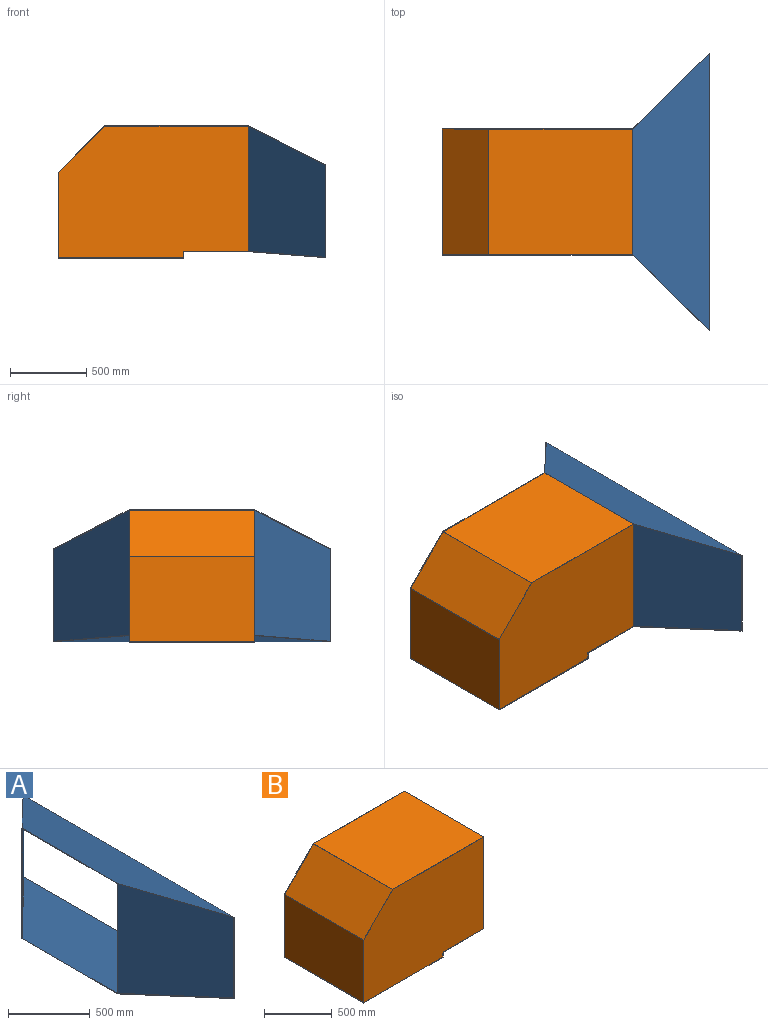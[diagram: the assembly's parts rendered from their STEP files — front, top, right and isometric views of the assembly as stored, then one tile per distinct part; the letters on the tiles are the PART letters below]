
ASSEMBLY  parts=2 mates=1
PART A: 10 faces, bbox 508x1823.4x867.1 mm
  f0: plane 1823.45x609.6mm, normal (1,0,0), area 14137.2mm2, adj f2,f3,f4,f5,f6,f7,f8,f9
  f1: plane 827.09x827.09mm, normal (-1,0,0), area 10308.9mm2, adj f2,f3,f4,f5,f6,f7,f8,f9
  f2: plane 1823.45x508mm, normal (0.45,0,0.89), area 754756.4mm2, adj f0,f1,f3,f5
  f3: plane 867.05x508mm, normal (-0.7,-0.71,0), area 511108.9mm2, adj f0,f1,f2,f4
  f4: plane 1823.45x508mm, normal (-0.08,0,-1), area 675315.6mm2, adj f0,f1,f3,f5
  f5: plane 867.05x508mm, normal (-0.7,0.71,0), area 511108.9mm2, adj f0,f1,f2,f4
  f6: plane 1816.33x508mm, normal (-0.45,0,-0.89), area 750704.3mm2, adj f0,f1,f7,f9
  f7: plane 861.66x508mm, normal (0.7,0.71,0), area 507270mm2, adj f0,f1,f6,f8
  f8: plane 1816.33x508mm, normal (0.08,0,1), area 671689.9mm2, adj f0,f1,f7,f9
  f9: plane 861.66x508mm, normal (0.7,-0.71,0), area 507270mm2, adj f0,f1,f6,f8
PART B: 18 faces, bbox 1251.7x827.1x870.7 mm
  f0: plane 827.09x827.09mm, normal (1,0,0), area 8377.4mm2, adj f2,f3,f4,f6,f10,f11,f12,f14
  f1: plane 827.09x827.09mm, normal (0,0,-1), area 159107mm2, adj f4,f5,f6,f7,f17
  f2: plane 946.94x827.09mm, normal (0,0,1), area 783205.3mm2, adj f0,f4,f6,f8
  f3: plane 827.09x424.66mm, normal (0,0,-1), area 351227.9mm2, adj f0,f4,f5,f6
  f4: plane 1251.74x870.74mm, normal (0,1,0), area 1024957.6mm2, adj f0,f1,f2,f3,f5,f7,f8
  f5: plane 827.09x43.66mm, normal (1,0,0), area 36107.5mm2, adj f1,f3,f4,f6
  f6: plane 1251.74x870.74mm, normal (0,-1,0), area 1024957.6mm2, adj f0,f1,f2,f3,f5,f7,f8
  f7: plane 827.09x565.94mm, normal (-1,0,0), area 468085mm2, adj f1,f4,f6,f8
  f8: plane 827.09x304.8mm, normal (-0.71,0,0.71), area 356518mm2, adj f2,f4,f6,f7
  f9: plane 822.01x822.01mm, normal (0,0,1), area 150729.6mm2, adj f12,f13,f14,f15,f17
  f10: plane 945.89x822.01mm, normal (0,0,-1), area 777530mm2, adj f0,f12,f14,f16
  f11: plane 822.01x427.2mm, normal (0,0,1), area 351158.5mm2, adj f0,f12,f13,f14
  f12: plane 1249.2x865.66mm, normal (0,-1,0), area 1016741.5mm2, adj f0,f9,f10,f11,f13,f15,f16
  f13: plane 822.01x43.66mm, normal (-1,0,0), area 35885.8mm2, adj f9,f11,f12,f14
  f14: plane 1249.2x865.66mm, normal (0,1,0), area 1016741.5mm2, adj f0,f9,f10,f11,f13,f15,f16
  f15: plane 822.01x562.35mm, normal (1,0,0), area 462257.3mm2, adj f9,f12,f14,f16
  f16: plane 822.01x303.31mm, normal (0.71,0,-0.71), area 352598.5mm2, adj f10,f12,f14,f15
  f17: cylinder r=408.78mm len=817.56mm, axis (0,0,-1), area 6523.9mm2, adj f1,f9
PLACE A t=(0,0,-9.79)mm
PLACE B t=(0,0,-9.94)mm
MATE fastened B.f0 <-> A.f1  axis (1,0,0) through (838.2,0,4409.66)mm
